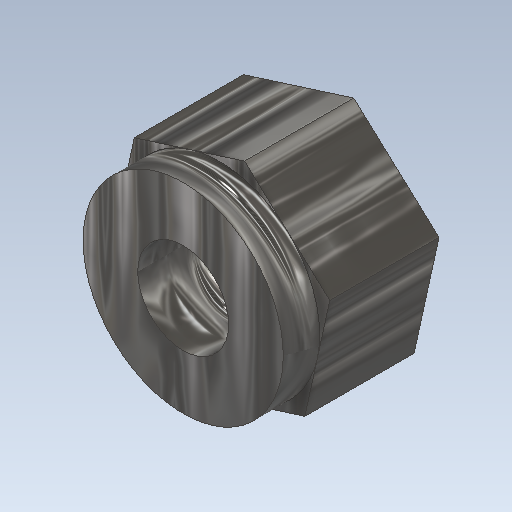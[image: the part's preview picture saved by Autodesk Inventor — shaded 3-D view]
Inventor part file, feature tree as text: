
AUTODESK INVENTOR PART (.ipt)
format: ipt  version: 2020.2 (Build 242310000, 310)  size: 212,480 bytes
history: native  units: mm
features: extrude x2, hole x2, other x1, sketch x1
ambient origin geometry x8: Origin, YZ Plane, XZ Plane, XY Plane, X Axis, Y Axis, Z Axis, Center Point
bodies: Body1 (feature_tree)
feature tree (6):
  other  "ソリッド1"
  sketch  "スケッチ1"
  extrude  "押し出し1"  Depth=6.350853mm
  extrude  "押し出し2"  Depth=5.5mm
  hole  "穴1"  [1 undecoded]
  hole  "穴2"  [1 undecoded]
note: 2 required parameter values undecoded (feature->parameter linkage not recoverable at this tier; creation-order binding heuristic only, values carry confidence <= 0.55)
